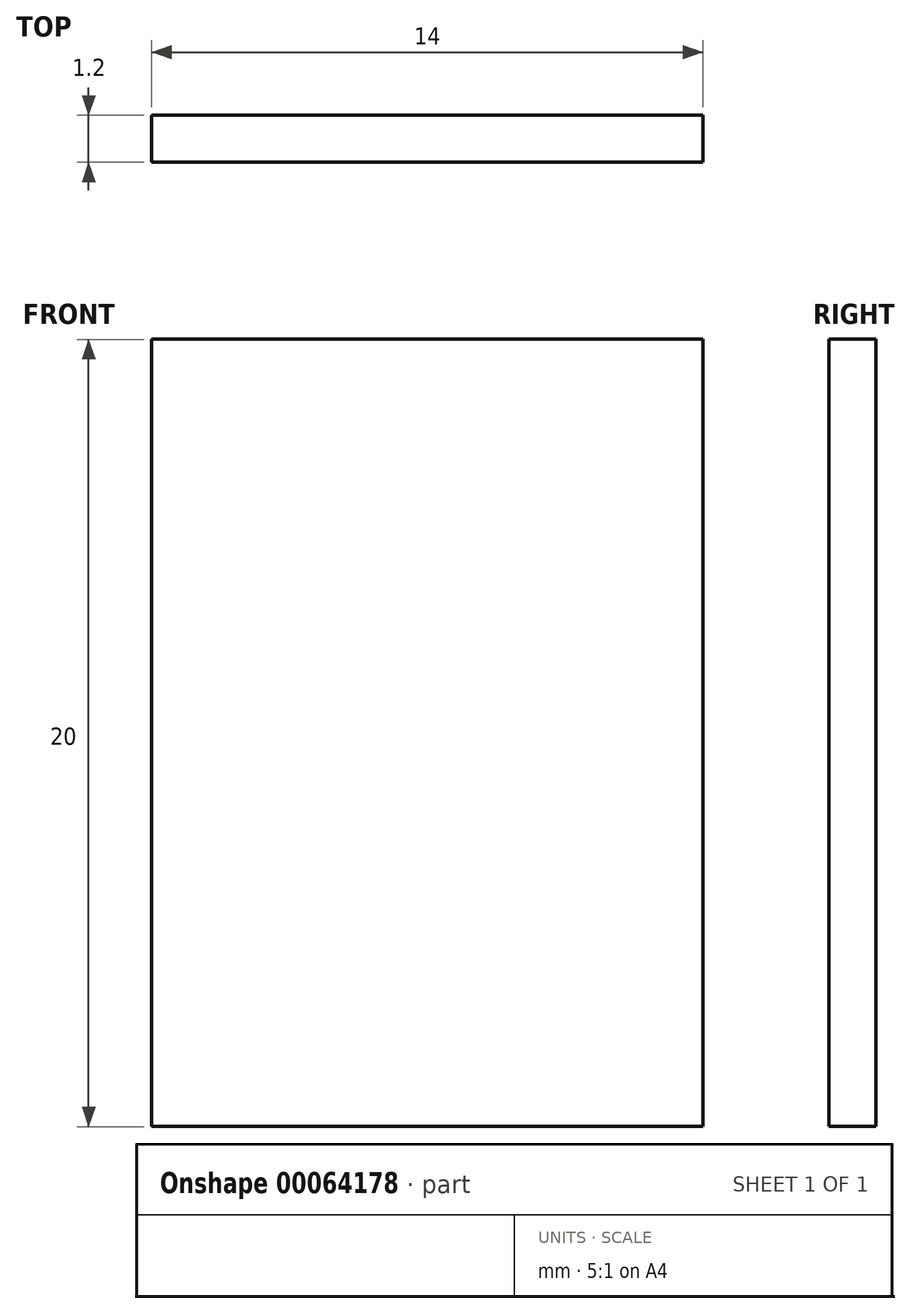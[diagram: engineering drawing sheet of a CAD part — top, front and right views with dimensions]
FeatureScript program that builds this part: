
annotation { "Feature Type Name" : "Feature", "Feature Type Description" : "" }
export const myFeature = defineFeature(function(context is Context, id is Id, definition is map)
    precondition{}
    {
        {
            var Q0;
            Q0=qCreatedBy(makeId("Front.planeOp"),FACE);
            var sketch = newSketch(context, id + "F0", { "sketchPlane" : qUnion([Q0])});
            skLineSegment(sketch, "E0.bottom", {"start": v(-6.52, 8.52) * mm, "end": v(7.48, 8.52) * mm});
            skLineSegment(sketch, "E0.top", {"start": v(-6.52, -11.48) * mm, "end": v(7.48, -11.48) * mm});
            skLineSegment(sketch, "E0.left", {"start": v(-6.52, 8.52) * mm, "end": v(-6.52, -11.48) * mm});
            skLineSegment(sketch, "E0.right", {"start": v(7.48, 8.52) * mm, "end": v(7.48, -11.48) * mm});
            skSolve(sketch);
        }
        {
            var Q0;
            Q0 = qSketchRegion(id + "F0", true);
            extrude(context, id + "F1", {"entities" : qUnion([Q0]), "depth" : 1.2 * mm});
        }
    });
